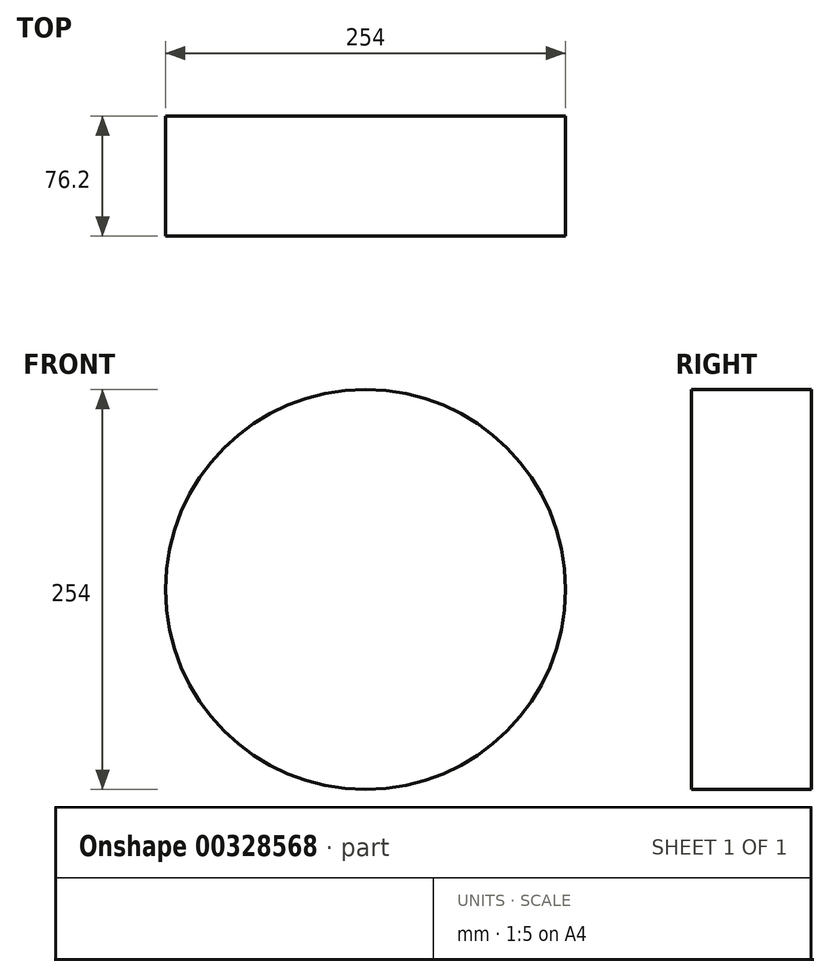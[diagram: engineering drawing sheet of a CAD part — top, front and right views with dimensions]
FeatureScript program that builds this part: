
annotation { "Feature Type Name" : "Feature", "Feature Type Description" : "" }
export const myFeature = defineFeature(function(context is Context, id is Id, definition is map)
    precondition{}
    {
        {
            var Q0;
            Q0=qCreatedBy(makeId("Front.planeOp"),FACE);
            var sketch = newSketch(context, id + "F0", { "sketchPlane" : qUnion([Q0])});
            skCircle(sketch, "E0", {"center": v(-1512.99, 0) * mm, "radius": 127 * mm});
            skSolve(sketch);
        }
        {
            var Q0;
            Q0=makeQuery(id+"F0.imprint","IMPRINT",FACE,{"disambiguationData":[TD([[makeQuery(id+"F0.imprint","IMPRINT",EDGE,{"derivedFrom":sQuery(id+"F0.wireOp",EDGE,"E0")}),1.0]])]});
            extrude(context, id + "F1", {"entities" : qUnion([Q0]), "depth" : 76.2 * mm});
        }
    });
